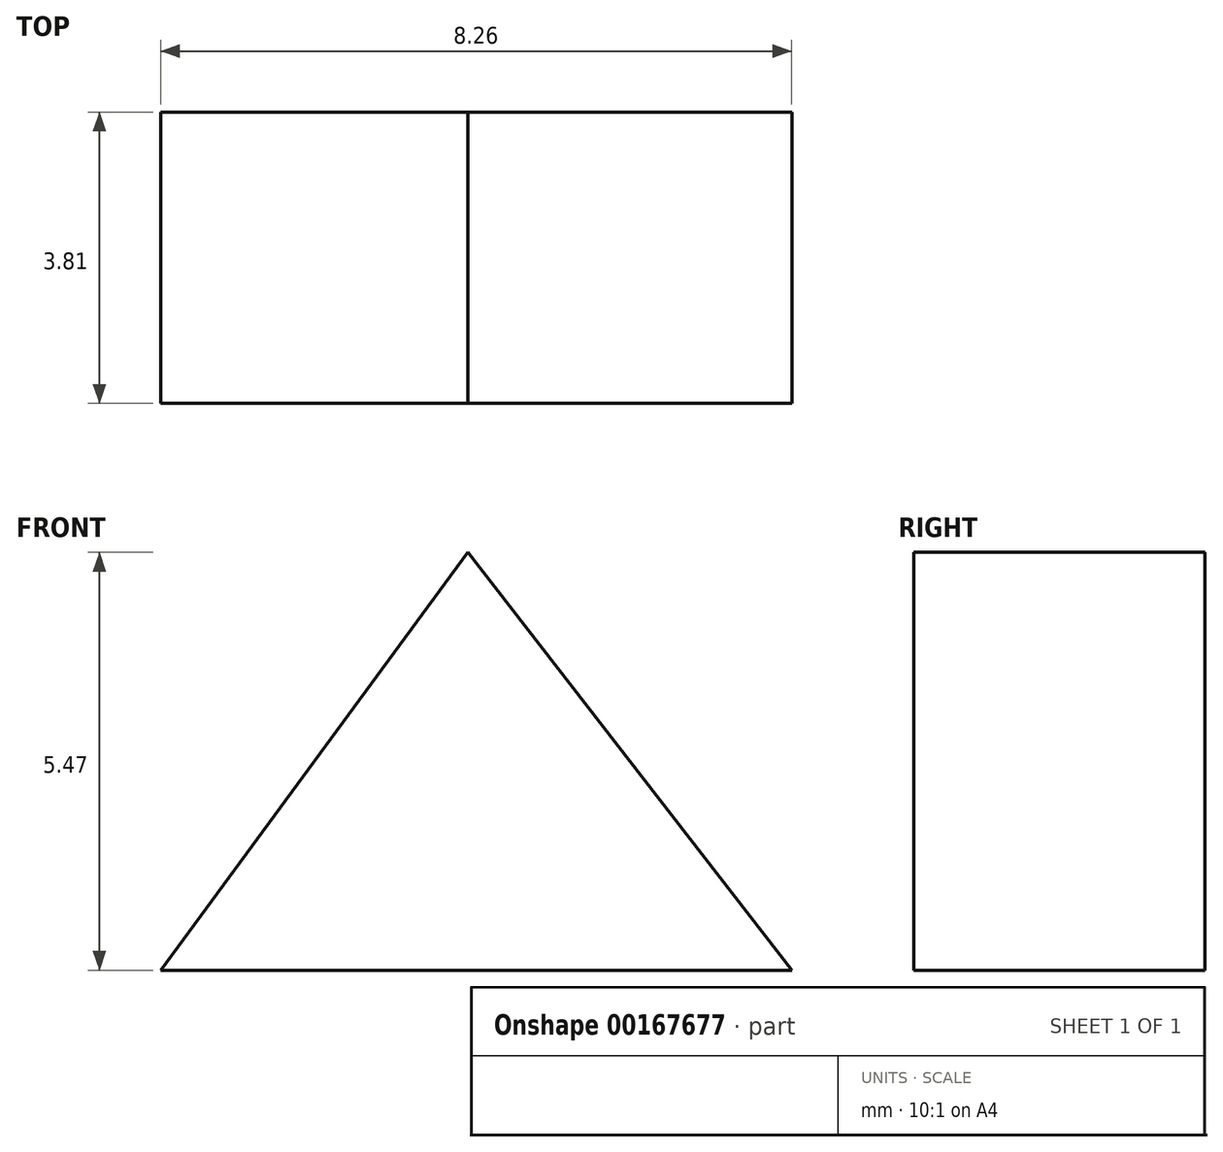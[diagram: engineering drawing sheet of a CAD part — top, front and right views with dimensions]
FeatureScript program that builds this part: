
annotation { "Feature Type Name" : "Feature", "Feature Type Description" : "" }
export const myFeature = defineFeature(function(context is Context, id is Id, definition is map)
    precondition{}
    {
        {
            var Q0;
            Q0=qCreatedBy(makeId("Front.planeOp"),FACE);
            var sketch = newSketch(context, id + "F0", { "sketchPlane" : qUnion([Q0])});
            skLineSegment(sketch, "E0", {"start": v(-4.02, 0) * mm, "end": v(4.24, 0) * mm});
            skLineSegment(sketch, "E1", {"start": v(4.24, 0) * mm, "end": v(0, 5.47) * mm});
            skLineSegment(sketch, "E2", {"start": v(0, 5.47) * mm, "end": v(-4.02, 0) * mm});
            skSolve(sketch);
        }
        {
            var Q0;
            Q0 = qSketchRegion(id + "F0", true);
            var Q1;
            Q1=makeQuery(id+"F0.imprint","IMPRINT",FACE,{"disambiguationData":[TD([[makeQuery(id+"F0.imprint","IMPRINT",EDGE,{"derivedFrom":sQuery(id+"F0.wireOp",EDGE,"E0")}),1.0]])]});
            extrude(context, id + "F1", {"entities" : qUnion([Q0, Q1]), "depth" : 3.8 * mm});
        }
    });
